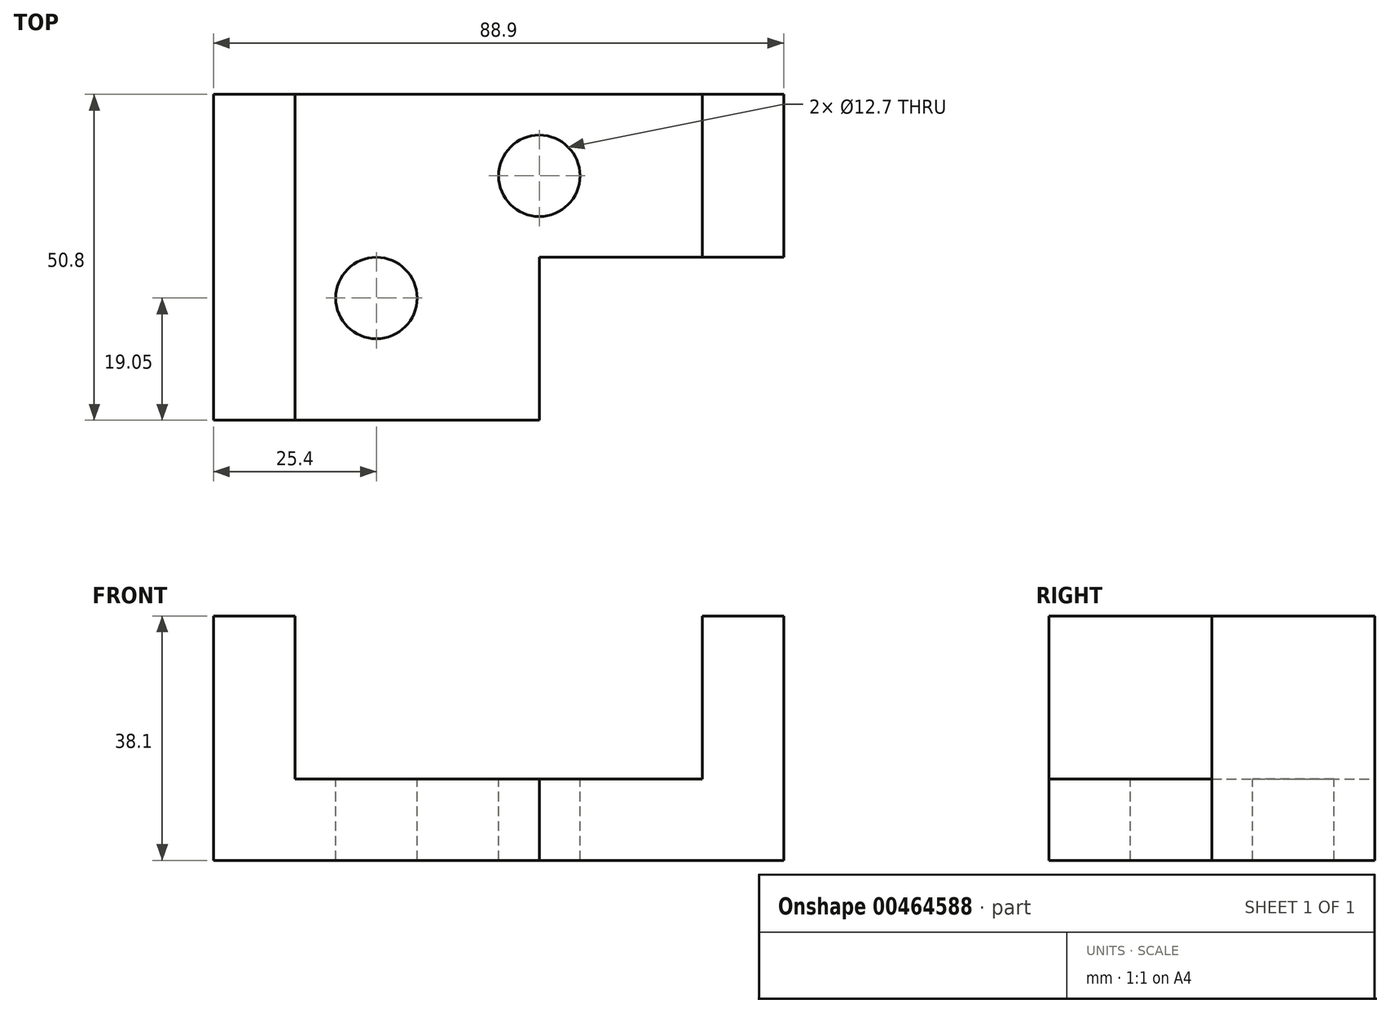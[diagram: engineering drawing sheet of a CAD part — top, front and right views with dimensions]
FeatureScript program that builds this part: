
annotation { "Feature Type Name" : "Feature", "Feature Type Description" : "" }
export const myFeature = defineFeature(function(context is Context, id is Id, definition is map)
    precondition{}
    {
        {
            var Q0;
            Q0=qCreatedBy(makeId("Front.planeOp"),FACE);
            var sketch = newSketch(context, id + "F0", { "sketchPlane" : qUnion([Q0])});
            skLineSegment(sketch, "E0.bottom", {"start": v(-44.45, 19.05) * mm, "end": v(44.45, 19.05) * mm});
            skLineSegment(sketch, "E0.top", {"start": v(-44.45, -19.05) * mm, "end": v(44.45, -19.05) * mm});
            skLineSegment(sketch, "E0.left", {"start": v(-44.45, 19.05) * mm, "end": v(-44.45, -19.05) * mm});
            skLineSegment(sketch, "E0.right", {"start": v(44.45, 19.05) * mm, "end": v(44.45, -19.05) * mm});
            skPoint(sketch, "E0.middle", {"position": v(0, 0) * mm});
            skSolve(sketch);
        }
        {
            var Q0;
            Q0=qSketchRegion(id+"F0",true);
            extrude(context, id + "F1", {"entities" : qUnion([Q0]), "depth" : 50.8 * mm});
        }
        {
            var Q0;
            Q0=makeQuery(id+"F1.opExtrude","SWEPT_FACE",FACE,{"disambiguationData":[OSD([sQuery(id+"F0.wireOp",EDGE,"E0.bottom")])]});
            var sketch = newSketch(context, id + "F2", { "sketchPlane" : qUnion([Q0])});
            skLineSegment(sketch, "E1.bottom", {"start": v(-31.75, -50.8) * mm, "end": v(31.75, -50.8) * mm});
            skLineSegment(sketch, "E1.top", {"start": v(-31.75, 0) * mm, "end": v(31.75, 0) * mm});
            skLineSegment(sketch, "E1.left", {"start": v(-31.75, -50.8) * mm, "end": v(-31.75, 0) * mm});
            skLineSegment(sketch, "E1.right", {"start": v(31.75, -50.8) * mm, "end": v(31.75, 0) * mm});
            skPoint(sketch, "E1.middle", {"position": v(0, -25.4) * mm});
            skSolve(sketch);
        }
        {
            var Q0;
            Q0=qSketchRegion(id+"F2",true);
            extrude(context, id + "F3", {"entities" : qUnion([Q0]), "operationType" : NewBodyOperationType.REMOVE, "oppositeDirection" : true, "depth" : 25.4 * mm});
        }
        {
            var Q0;
            Q0=makeQuery(id+"F1.opExtrude","SWEPT_FACE",FACE,{"disambiguationData":[OSD([sQuery(id+"F0.wireOp",EDGE,"E0.right")])]});
            var sketch = newSketch(context, id + "F4", { "sketchPlane" : qUnion([Q0])});
            skLineSegment(sketch, "E2.bottom", {"start": v(-50.8, 19.05) * mm, "end": v(-25.4, 19.05) * mm});
            skLineSegment(sketch, "E2.top", {"start": v(-50.8, -19.05) * mm, "end": v(-25.4, -19.05) * mm});
            skLineSegment(sketch, "E2.left", {"start": v(-50.8, 19.05) * mm, "end": v(-50.8, -19.05) * mm});
            skLineSegment(sketch, "E2.right", {"start": v(-25.4, 19.05) * mm, "end": v(-25.4, -19.05) * mm});
            skSolve(sketch);
        }
        {
            var Q0;
            Q0=qSketchRegion(id+"F4",true);
            extrude(context, id + "F5", {"entities" : qUnion([Q0]), "operationType" : NewBodyOperationType.REMOVE, "oppositeDirection" : true, "depth" : 38.1 * mm});
        }
        {
            var Q0;
            Q0=makeQuery(id+"F3.boolean.opBoolean","COPY",FACE,{"derivedFrom":makeQuery(id+"F3.opExtrude","CAP_FACE",FACE,{"disambiguationData":[OSD([sQuery(id+"F2.wireOp",EDGE,"E1.bottom"),sQuery(id+"F2.wireOp",EDGE,"E1.top"),sQuery(id+"F2.wireOp",EDGE,"E1.left"),sQuery(id+"F2.wireOp",EDGE,"E1.right")])],"isStart":false})});
            var sketch = newSketch(context, id + "F6", { "sketchPlane" : qUnion([Q0])});
            skCircle(sketch, "E3", {"center": v(-19.05, -31.75) * mm, "radius": 6.35 * mm});
            skCircle(sketch, "E4", {"center": v(6.35, -12.7) * mm, "radius": 6.35 * mm});
            skSolve(sketch);
        }
        {
            var Q0;
            Q0=qSketchRegion(id+"F6",true);
            extrude(context, id + "F7", {"entities" : qUnion([Q0]), "operationType" : NewBodyOperationType.REMOVE, "oppositeDirection" : true, "depth" : 25.4 * mm});
        }
    });
